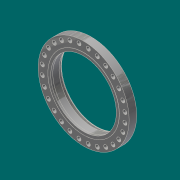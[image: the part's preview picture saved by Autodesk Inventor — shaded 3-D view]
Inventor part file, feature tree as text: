
AUTODESK INVENTOR PART (.ipt)
format: ipt  version: 2017.3 (Build 213257000, 257)  size: 378,880 bytes
history: native  units: in
note: dims shown in document units (in); Inventor stores cm internally (conversion verified against a paired STEP export)
features: sketch x6, extrude x4, chamfer x4, fillet x2, hole x1, pattern_circular x1, revolve x1, projected_geometry x1
ambient origin geometry x8: Origin, YZ Plane, XZ Plane, XY Plane, X Axis, Y Axis, Z Axis, Center Point
bodies: Solid1 (feature_tree)
feature tree (20):
  extrude  "Extrusion1"  Depth=31.0in
  extrude  "Extrusion2"  Depth=3.625in
  extrude  "Extrusion3"  Depth=0.0625in
  extrude  "Extrusion9"  Depth=19.625in
  hole  "Hole1"  [1 undecoded]
  chamfer  "Chamfer3"  Distance=0.0625in
  pattern_circular  "Circular Pattern1"  [2 undecoded]
  chamfer  "Chamfer2"  Distance=0.0312in Angle=45.0deg
  fillet  "Fillet2"  Radius=0.0625in
  chamfer  "Chamfer4"  Distance=34.0in
  revolve  "Revolution3"  [1 undecoded]
  fillet  "Fillet7"  Radius=0.125in
  chamfer  "Chamfer8"  Distance=0.25in
  sketch  "Sketch1"  dims[d0=43.0in d1=31.0in]
  sketch  "Sketch2"  dims[d2=3.625in d3=0.0in d4=33.75in]
  sketch  "Sketch3"  dims[d5=0.0625in d6=0.0in d7=34.75in]
  sketch  "Sketch4"  dims[d8=2.4375in d9=0.0in d13=19.625in]
  sketch  "Sketch12"  dims[d14=0.0442in]
  sketch  "Sketch15"  dims[d15=1.875in d16=0.75in d17=0.375in d18=0.25in d19=0.5635in d20=1.0in d21=0.8108in d22=11.0236in d23=360.0deg d25=0.0625in d26=0.125in d27=0.0687in d29=0.4375in d30=0.0312in d31=0.125in d32=45.0deg d33=0.0625in d34=0.125in d35=45.0deg d98=34.0in d99=0.3125in d100=0.125in d101=0.25in d102=0.2577in d103=0.5in d104=0.875in d105=0.3852in d106=31.375in d108=90.0deg d109=0.0312in d110=0.0312in d111=0.125in d112=45.0deg d120=1.0in d129=1.0in d130=0.0in d134=0.0625in d135=0.1718in]
  projected_geometry  "Projected Loop1"
note: 4 required parameter values undecoded (feature->parameter linkage not recoverable at this tier; creation-order binding heuristic only, values carry confidence <= 0.55)